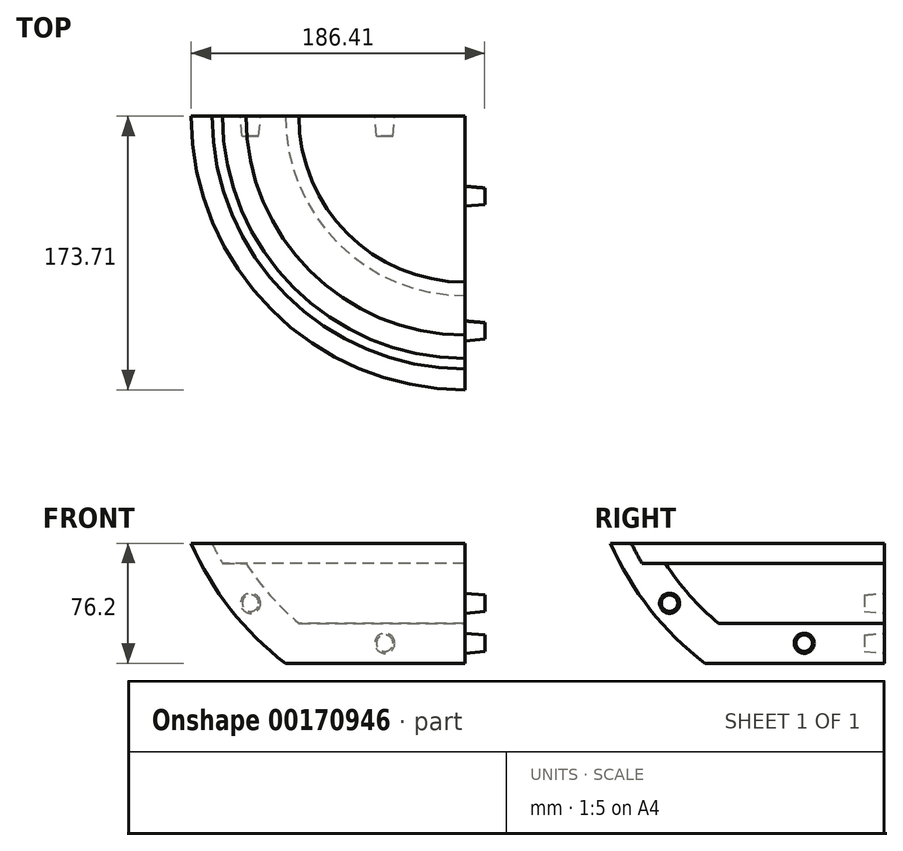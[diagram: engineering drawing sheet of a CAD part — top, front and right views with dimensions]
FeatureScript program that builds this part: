
annotation { "Feature Type Name" : "Feature", "Feature Type Description" : "" }
export const myFeature = defineFeature(function(context is Context, id is Id, definition is map)
    precondition{}
    {
        {
            var Q0;
            Q0=qCreatedBy(makeId("Front.planeOp"),FACE);
            var sketch = newSketch(context, id + "F0", { "sketchPlane" : qUnion([Q0])});
            skArc(sketch, "E0", {"start": v(-83.77, -157.78) * mm, "mid": v(-80.56, -164.2) * mm, "end": v(-77.1, -170.48) * mm});
            skLineSegment(sketch, "E1", {"start": v(-28.6, -208.58) * mm, "end": v(76.74, -208.58) * mm});
            skArc(sketch, "E2", {"start": v(-62.24, -170.48) * mm, "mid": v(-46.9, -190.83) * mm, "end": v(-28.6, -208.58) * mm});
            skLineSegment(sketch, "E3", {"start": v(-77.1, -170.48) * mm, "end": v(-62.24, -170.48) * mm});
            skLineSegment(sketch, "E4", {"start": v(-37.16, -233.98) * mm, "end": v(76.74, -233.98) * mm});
            skLineSegment(sketch, "E5", {"start": v(76.74, -233.98) * mm, "end": v(76.74, -208.58) * mm});
            skLineSegment(sketch, "E6", {"start": v(-83.77, -157.78) * mm, "end": v(-96.97, -157.78) * mm});
            skArc(sketch, "E7", {"start": v(-96.97, -157.78) * mm, "mid": v(-71.98, -199.74) * mm, "end": v(-37.16, -233.98) * mm});
            skSolve(sketch);
        }
        {
            var Q0;
            Q0=makeQuery(id+"F0.imprint","IMPRINT",FACE,{"disambiguationData":[TD([[makeQuery(id+"F0.imprint","IMPRINT",EDGE,{"derivedFrom":sQuery(id+"F0.wireOp",EDGE,"E0")}),-1.0]])]});
            var Q1;
            Q1=sQuery(id+"F0.wireOp",EDGE,"E5");
            revolve(context, id + "F1", {"entities" : qUnion([Q0]), "axis" : qUnion([Q1]), "revolveType" : RevolveType.ONE_DIRECTION, "angle" : 90 * degree});
        }
        {
            var Q0;
            Q0=makeQuery(id+"F1.opRevolve","CAP_FACE",FACE,{"disambiguationData":[OSD([sQuery(id+"F0.wireOp",EDGE,"127faa61-2dd5-4f04-9b80-e974ed59e8e2"),sQuery(id+"F0.wireOp",EDGE,"63b47105-3ce9-4c21-bbef-0bde87c7e84d"),sQuery(id+"F0.wireOp",EDGE,"3f866c7a-0179-43e7-bfb8-e1e3094c20ca"),sQuery(id+"F0.wireOp",EDGE,"E0"),sQuery(id+"F0.wireOp",EDGE,"7CH24ke3-2Y0P-gIKA-winm-9kQa9B6rmt9s"),sQuery(id+"F0.wireOp",EDGE,"aH0l3RZl-ftT6-iEtQ-Z4w5-QL9ypOhPZTW7"),sQuery(id+"F0.wireOp",EDGE,"AQcdqtHQ-1qCl-9p5w-JLKS-hNKEzMtKLlJM"),sQuery(id+"F0.wireOp",EDGE,"8799a0c3-f370-4d08-a085-7c9c70e67373.trimOffspring")])],"isStart":false});
            var sketch = newSketch(context, id + "F2", { "sketchPlane" : qUnion([Q0])});
            skCircle(sketch, "E8", {"center": v(-136.34, -195.88) * mm, "radius": 6.35 * mm});
            skCircle(sketch, "E9", {"center": v(-50.8, -221.28) * mm, "radius": 6.35 * mm});
            skSolve(sketch);
        }
        {
            var Q0;
            Q0=makeQuery(id+"F2.imprint","IMPRINT",FACE,{"disambiguationData":[TD([[makeQuery(id+"F2.imprint","IMPRINT",EDGE,{"derivedFrom":sQuery(id+"F2.wireOp",EDGE,"E8")}),1.0]])]});
            var Q1;
            Q1=makeQuery(id+"F2.imprint","IMPRINT",FACE,{"disambiguationData":[TD([[makeQuery(id+"F2.imprint","IMPRINT",EDGE,{"derivedFrom":sQuery(id+"F2.wireOp",EDGE,"E9")}),1.0]])]});
            extrude(context, id + "F3", {"entities" : qUnion([Q0, Q1]), "operationType" : NewBodyOperationType.ADD, "depth" : 12.7 * mm, "hasDraft" : true, "draftAngle" : 5 * degree, "draftPullDirection" : true});
        }
        {
            var Q0;
            Q0=makeQuery(id+"F1.opRevolve","CAP_FACE",FACE,{"disambiguationData":[OSD([sQuery(id+"F0.wireOp",EDGE,"63b47105-3ce9-4c21-bbef-0bde87c7e84d"),sQuery(id+"F0.wireOp",EDGE,"3f866c7a-0179-43e7-bfb8-e1e3094c20ca"),sQuery(id+"F0.wireOp",EDGE,"E0"),sQuery(id+"F0.wireOp",EDGE,"7CH24ke3-2Y0P-gIKA-winm-9kQa9B6rmt9s"),sQuery(id+"F0.wireOp",EDGE,"aH0l3RZl-ftT6-iEtQ-Z4w5-QL9ypOhPZTW7"),sQuery(id+"F0.wireOp",EDGE,"8799a0c3-f370-4d08-a085-7c9c70e67373.trimOffspring"),sQuery(id+"F0.wireOp",EDGE,"5GbaFhkx-Lqx5-JDGC-G8vW-frHXgwWoUHXO"),sQuery(id+"F0.wireOp",EDGE,"itz2tbXk-hzkF-TLTC-ZvAC-DheZIswQ2QX4")])],"isStart":true});
            var sketch = newSketch(context, id + "F4", { "sketchPlane" : qUnion([Q0])});
            skCircle(sketch, "E10", {"center": v(-25.94, -221.28) * mm, "radius": 6.35 * mm});
            skCircle(sketch, "E11", {"center": v(59.31, -195.88) * mm, "radius": 6.35 * mm});
            skSolve(sketch);
        }
        {
            var Q0;
            Q0 = qSketchRegion(id + "F4", true);
            extrude(context, id + "F5", {"entities" : qUnion([Q0]), "operationType" : NewBodyOperationType.REMOVE, "oppositeDirection" : true, "depth" : 12.7 * mm, "hasDraft" : true, "draftAngle" : 5 * degree, "draftPullDirection" : true});
        }
    });
